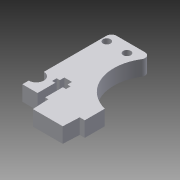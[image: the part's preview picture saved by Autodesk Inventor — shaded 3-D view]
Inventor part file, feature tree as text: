
AUTODESK INVENTOR PART (.ipt)
format: ipt  version: 2013 (Build 170138000, 138)  size: 109,568 bytes
history: native  units: mm
features: extrude x1, sketch x1
ambient origin geometry x8: Origin, YZ Plane, XZ Plane, XY Plane, X Axis, Y Axis, Z Axis, Center Point
bodies: Solid1 (feature_tree)
feature tree (2):
  extrude  "Extrusion1"  [1 undecoded]
  sketch  "Sketch1"  dims[d0=6.0mm d1=0.0mm]
note: 1 required parameter value undecoded (feature->parameter linkage not recoverable at this tier; creation-order binding heuristic only, values carry confidence <= 0.55)
